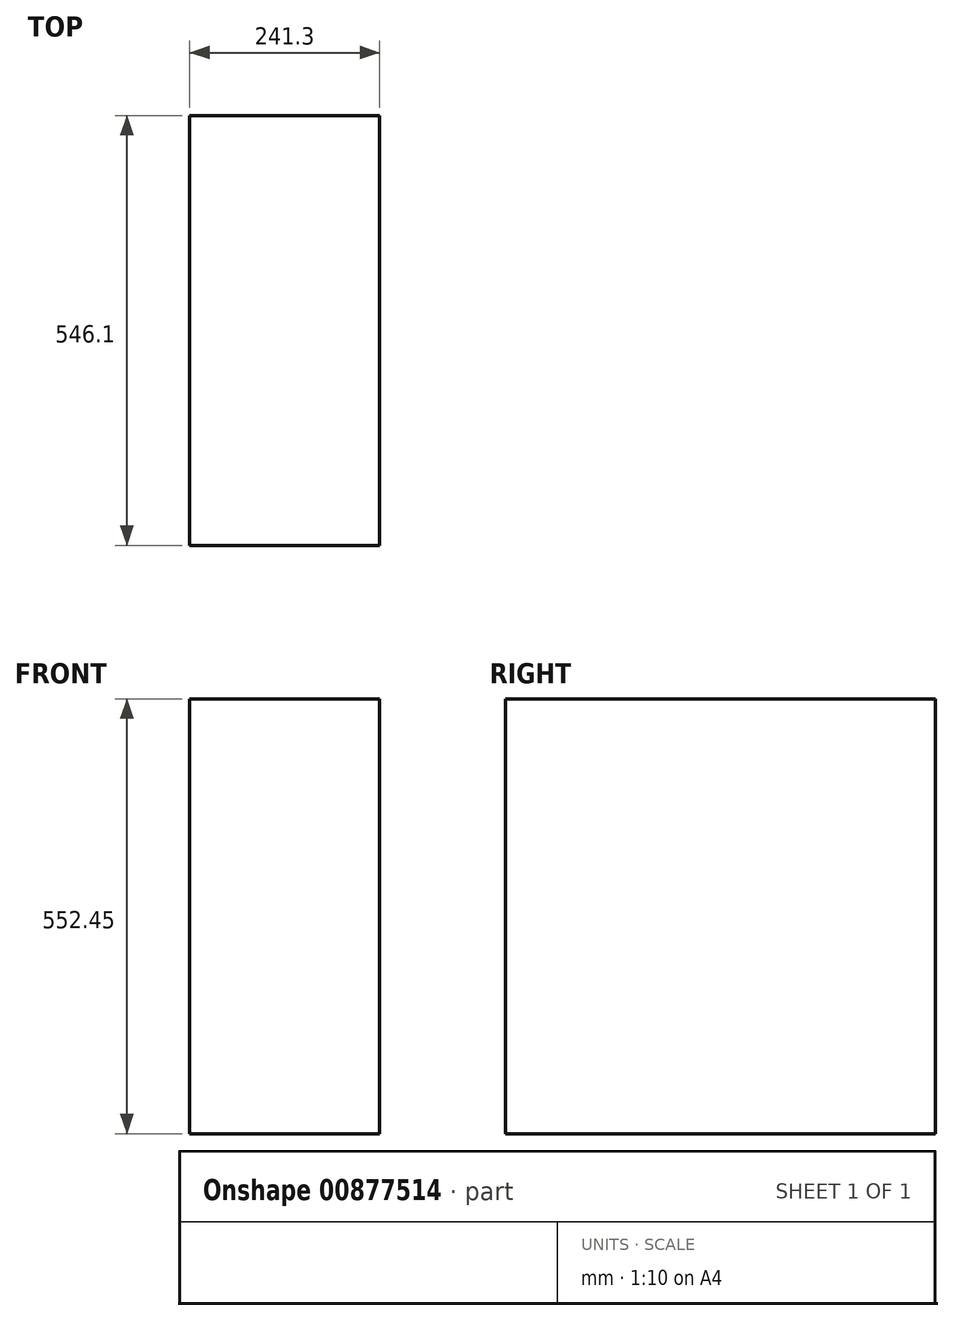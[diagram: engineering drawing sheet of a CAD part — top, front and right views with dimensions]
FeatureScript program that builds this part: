
annotation { "Feature Type Name" : "Feature", "Feature Type Description" : "" }
export const myFeature = defineFeature(function(context is Context, id is Id, definition is map)
    precondition{}
    {
        {
            var Q0;
            Q0=qCreatedBy(makeId("Top.planeOp"),FACE);
            var sketch = newSketch(context, id + "F0", { "sketchPlane" : qUnion([Q0])});
            skLineSegment(sketch, "E0.bottom", {"start": v(-120.65, 273.05) * mm, "end": v(120.65, 273.05) * mm});
            skLineSegment(sketch, "E0.top", {"start": v(-120.65, -273.05) * mm, "end": v(120.65, -273.05) * mm});
            skLineSegment(sketch, "E0.left", {"start": v(-120.65, 273.05) * mm, "end": v(-120.65, -273.05) * mm});
            skLineSegment(sketch, "E0.right", {"start": v(120.65, 273.05) * mm, "end": v(120.65, -273.05) * mm});
            skPoint(sketch, "E0.middle", {"position": v(0, 0) * mm});
            skSolve(sketch);
        }
        {
            var Q0;
            Q0 = qSketchRegion(id + "F0", true);
            extrude(context, id + "F1", {"entities" : qUnion([Q0]), "depth" : 552.45 * mm, "offsetDistance" : 25.4 * mm});
        }
    });
